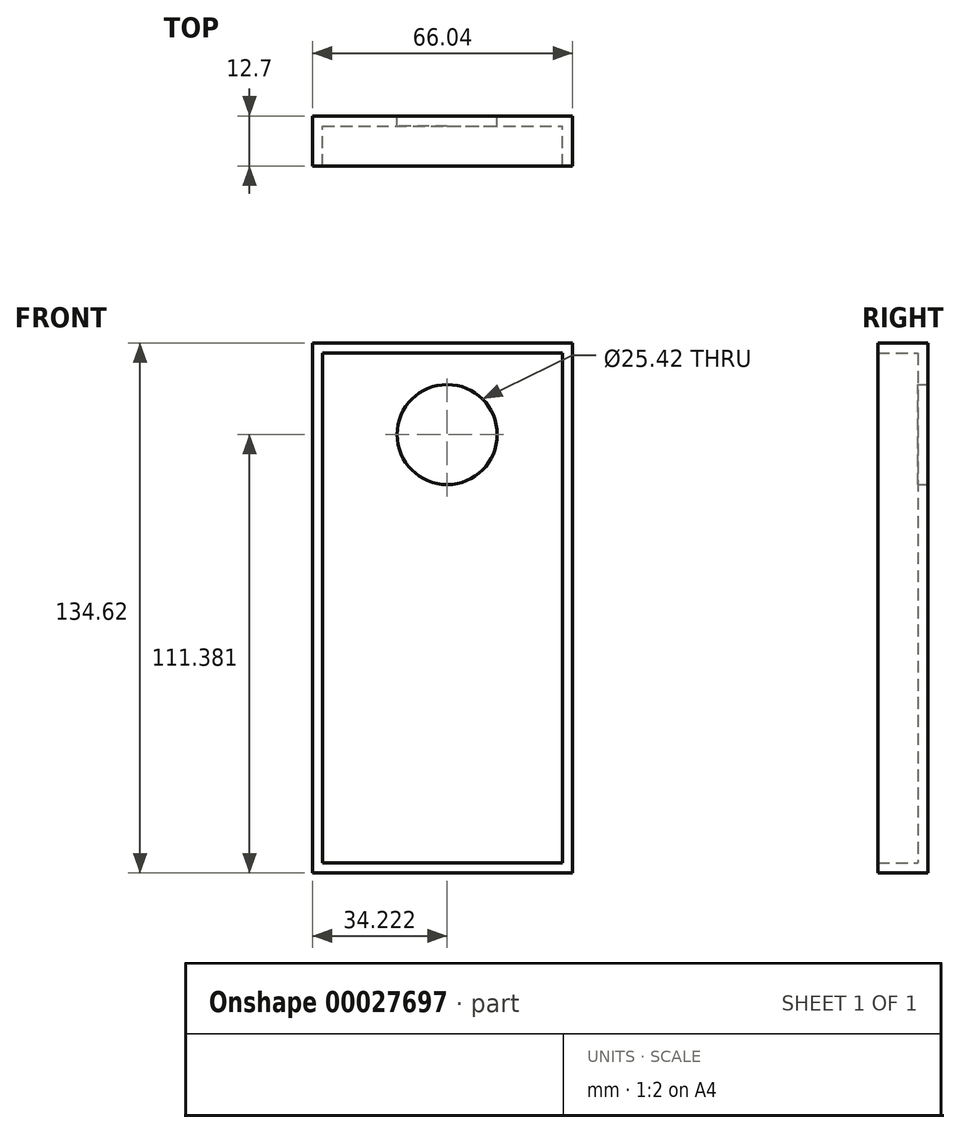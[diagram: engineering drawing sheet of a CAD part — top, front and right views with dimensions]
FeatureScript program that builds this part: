
annotation { "Feature Type Name" : "Feature", "Feature Type Description" : "" }
export const myFeature = defineFeature(function(context is Context, id is Id, definition is map)
    precondition{}
    {
        {
            var Q0;
            Q0=qCreatedBy(makeId("Front.planeOp"),FACE);
            var sketch = newSketch(context, id + "F0", { "sketchPlane" : qUnion([Q0])});
            skLineSegment(sketch, "E0.bottom", {"start": v(-43.35, 62.46) * mm, "end": v(22.69, 62.46) * mm});
            skLineSegment(sketch, "E0.top", {"start": v(-43.35, -72.16) * mm, "end": v(22.69, -72.16) * mm});
            skLineSegment(sketch, "E0.left", {"start": v(-43.35, 62.46) * mm, "end": v(-43.35, -72.16) * mm});
            skLineSegment(sketch, "E0.right", {"start": v(22.69, 62.46) * mm, "end": v(22.69, -72.16) * mm});
            skSolve(sketch);
        }
        {
            var Q0;
            Q0=makeQuery(id+"F0.imprint","IMPRINT",FACE,{"disambiguationData":[TD([[makeQuery(id+"F0.imprint","IMPRINT",EDGE,{"derivedFrom":sQuery(id+"F0.wireOp",EDGE,"E0.bottom")}),-1.0]])]});
            extrude(context, id + "F1", {"entities" : qUnion([Q0]), "depth" : 12.7 * mm});
        }
        {
            var Q0;
            Q0=makeQuery(id+"F1.opExtrude","CAP_FACE",FACE,{"disambiguationData":[OSD([sQuery(id+"F0.wireOp",EDGE,"E0.bottom"),sQuery(id+"F0.wireOp",EDGE,"E0.top"),sQuery(id+"F0.wireOp",EDGE,"E0.left"),sQuery(id+"F0.wireOp",EDGE,"E0.right")])],"isStart":false});
            shell(context, id + "F2", {"entities" : qUnion([Q0]), "thickness" : 2.54 * mm});
        }
        {
            var Q0;
            Q0=makeQuery(id+"F1.opExtrude","CAP_FACE",FACE,{"disambiguationData":[OSD([sQuery(id+"F0.wireOp",EDGE,"E0.bottom"),sQuery(id+"F0.wireOp",EDGE,"E0.top"),sQuery(id+"F0.wireOp",EDGE,"E0.left"),sQuery(id+"F0.wireOp",EDGE,"E0.right")])],"isStart":true});
            var sketch = newSketch(context, id + "F3", { "sketchPlane" : qUnion([Q0])});
            skCircle(sketch, "E1", {"center": v(9.13, 39.22) * mm, "radius": 12.7 * mm});
            skSolve(sketch);
        }
        {
            var Q0;
            Q0=makeQuery(id+"F3.imprint","IMPRINT",FACE,{"disambiguationData":[TD([[makeQuery(id+"F3.imprint","IMPRINT",EDGE,{"derivedFrom":sQuery(id+"F3.wireOp",EDGE,"E1")}),1.0]])]});
            extrude(context, id + "F4", {"entities" : qUnion([Q0]), "operationType" : NewBodyOperationType.REMOVE, "oppositeDirection" : true, "depth" : 25.4 * mm});
        }
    });
